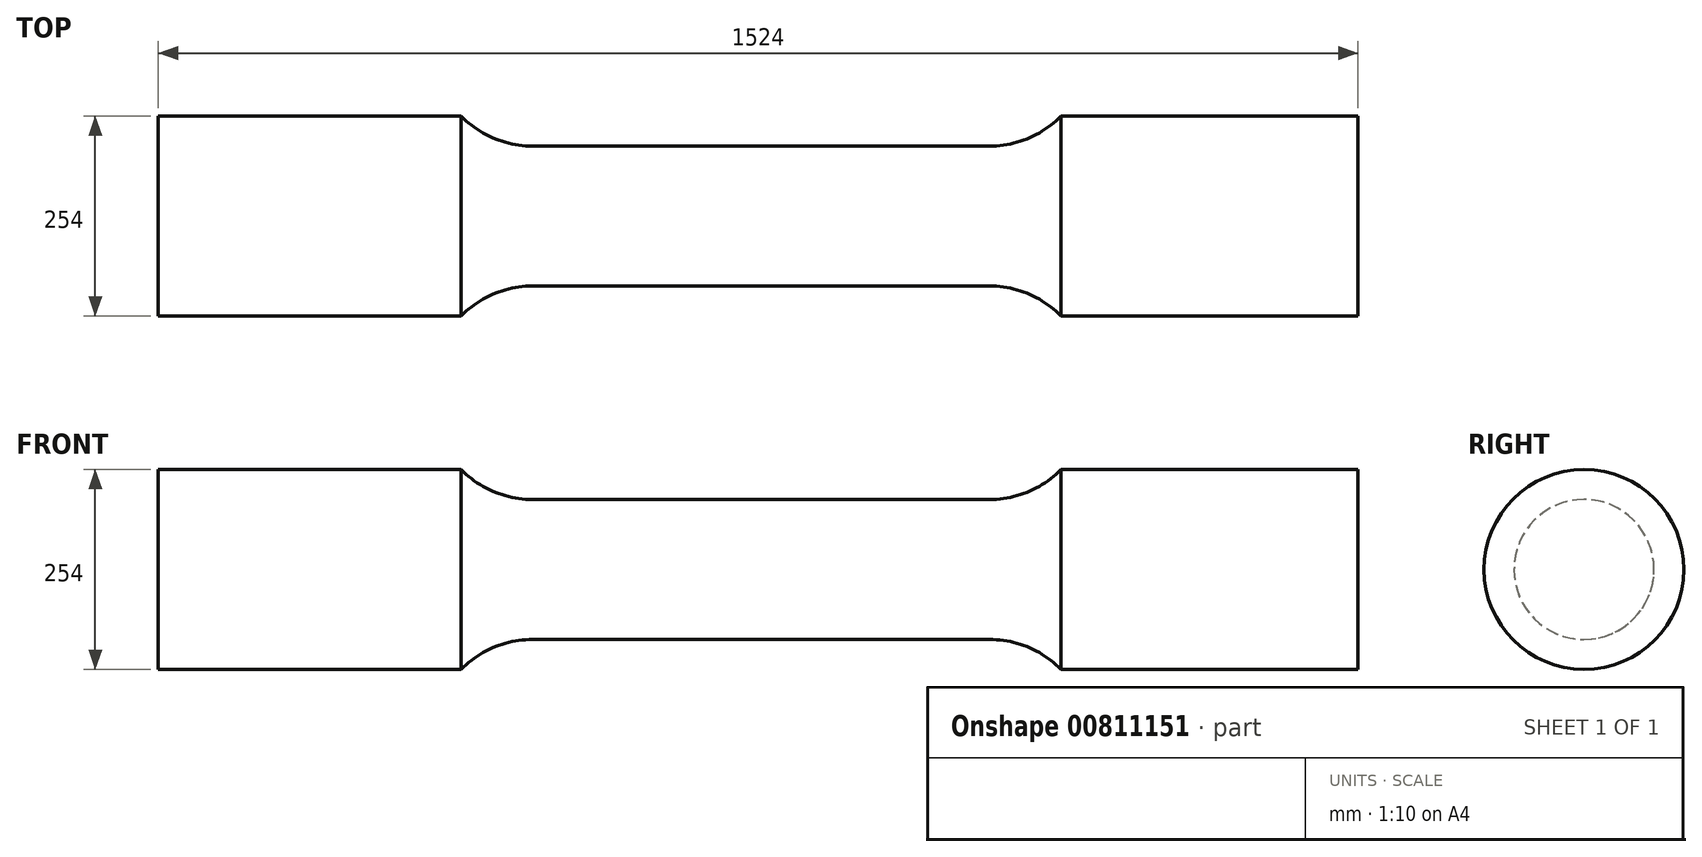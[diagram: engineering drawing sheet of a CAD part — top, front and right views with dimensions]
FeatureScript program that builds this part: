
annotation { "Feature Type Name" : "Feature", "Feature Type Description" : "" }
export const myFeature = defineFeature(function(context is Context, id is Id, definition is map)
    precondition{}
    {
        {
            var Q0;
            Q0=qCreatedBy(makeId("Front.planeOp"),FACE);
            var sketch = newSketch(context, id + "F0", { "sketchPlane" : qUnion([Q0])});
            skLineSegment(sketch, "E0.bottom", {"start": v(-633.13, 0) * mm, "end": v(890.87, 0) * mm});
            skLineSegment(sketch, "E0.top", {"start": v(-633.13, 127) * mm, "end": v(890.87, 127) * mm});
            skLineSegment(sketch, "E0.left", {"start": v(-633.13, 0) * mm, "end": v(-633.13, 127) * mm});
            skLineSegment(sketch, "E0.right", {"start": v(890.87, 0) * mm, "end": v(890.87, 127) * mm});
            skSolve(sketch);
        }
        {
            var Q0;
            Q0=makeQuery(id+"F0.imprint","IMPRINT",FACE,{"disambiguationData":[TD([[makeQuery(id+"F0.imprint","IMPRINT",EDGE,{"derivedFrom":sQuery(id+"F0.wireOp",EDGE,"E0.bottom")}),1.0]])]});
            var Q1;
            Q1=sQuery(id+"F0.wireOp",EDGE,"E0.bottom");
            revolve(context, id + "F1", {"surfaceOperationType" : NewSurfaceOperationType.NEW, "entities" : qUnion([Q0]), "axis" : qUnion([Q1]), "revolveType" : RevolveType.FULL});
        }
        {
            var Q0;
            Q0=qCreatedBy(makeId("Front.planeOp"),FACE);
            var sketch = newSketch(context, id + "F2", { "sketchPlane" : qUnion([Q0])});
            skLineSegment(sketch, "E1.bottom", {"start": v(-248.48, 394.44) * mm, "end": v(513.52, 394.44) * mm});
            skLineSegment(sketch, "E1.top", {"start": v(-248.48, 88.9) * mm, "end": v(513.52, 88.9) * mm});
            skLineSegment(sketch, "E1.left", {"start": v(-248.48, 394.44) * mm, "end": v(-248.48, 88.9) * mm});
            skLineSegment(sketch, "E1.right", {"start": v(513.52, 394.44) * mm, "end": v(513.52, 88.9) * mm});
            skLineSegment(sketch, "E2", {"start": v(-629.48, 0) * mm, "end": v(673.65, 0) * mm});
            skSolve(sketch);
        }
        {
            var Q0;
            Q0=makeQuery(id+"F2.imprint","IMPRINT",FACE,{"disambiguationData":[TD([[makeQuery(id+"F2.imprint","IMPRINT",EDGE,{"derivedFrom":sQuery(id+"F2.wireOp",EDGE,"E1.bottom")}),-1.0]])]});
            var Q1;
            Q1=sQuery(id+"F2.wireOp",EDGE,"E2");
            revolve(context, id + "F3", {"operationType" : NewBodyOperationType.REMOVE, "surfaceOperationType" : NewSurfaceOperationType.NEW, "entities" : qUnion([Q0]), "axis" : qUnion([Q1]), "revolveType" : RevolveType.FULL});
        }
        {
            var Q0;
            Q0=makeQuery(id+"F3.boolean.opBoolean","COPY",EDGE,{"derivedFrom":makeQuery(id+"F3.opRevolve","SWEPT_EDGE",EDGE,{"disambiguationData":[OSD([sQuery(id+"F2.wireOp",EDGE,"E1.top"),sQuery(id+"F2.wireOp",EDGE,"E1.left")])]})});
            fillet(context, id + "F4", {"entities" : qUnion([Q0]), "radius" : 127 * mm, "tangentPropagation" : true, "allowEdgeOverflow" : false});
        }
        {
            var Q0;
            Q0=makeQuery(id+"F3.boolean.opBoolean","COPY",EDGE,{"derivedFrom":makeQuery(id+"F3.opRevolve","SWEPT_EDGE",EDGE,{"disambiguationData":[OSD([sQuery(id+"F2.wireOp",EDGE,"E1.top"),sQuery(id+"F2.wireOp",EDGE,"E1.right")])]})});
            fillet(context, id + "F5", {"entities" : qUnion([Q0]), "radius" : 127 * mm, "tangentPropagation" : true, "allowEdgeOverflow" : false});
        }
    });
